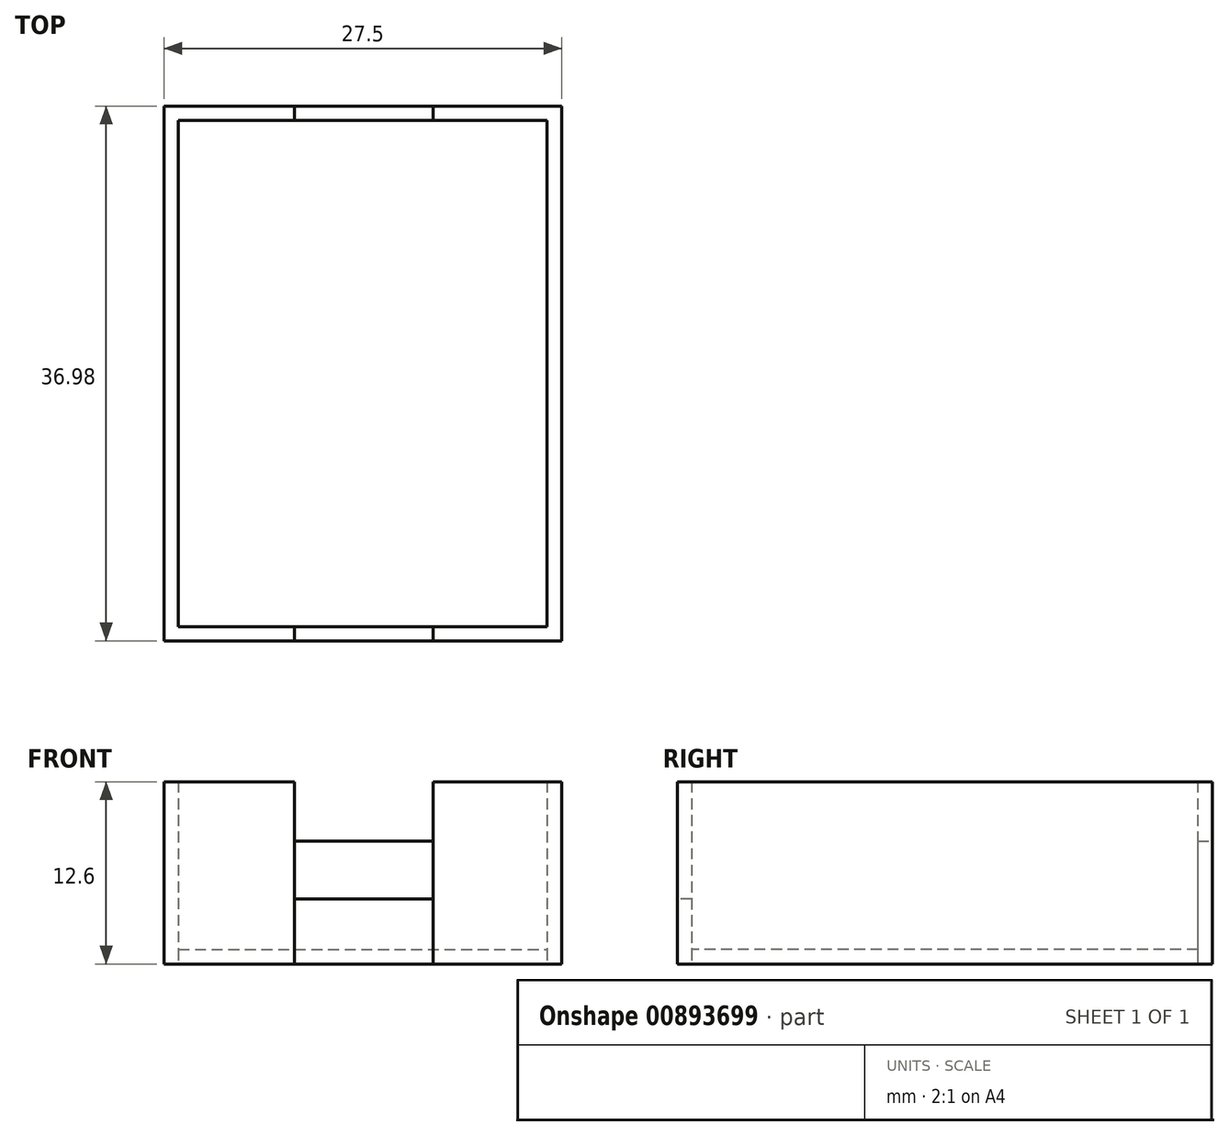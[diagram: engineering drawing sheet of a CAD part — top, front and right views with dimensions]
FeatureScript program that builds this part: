
annotation { "Feature Type Name" : "Feature", "Feature Type Description" : "" }
export const myFeature = defineFeature(function(context is Context, id is Id, definition is map)
    precondition{}
    {
        {
            var Q0;
            Q0=qCreatedBy(makeId("Top.planeOp"),FACE);
            var sketch = newSketch(context, id + "F0", { "sketchPlane" : qUnion([Q0])});
            skLineSegment(sketch, "E0.bottom", {"start": v(-11.86, 7.23) * mm, "end": v(13.64, 7.23) * mm});
            skLineSegment(sketch, "E0.top", {"start": v(-11.86, -27.77) * mm, "end": v(13.64, -27.77) * mm});
            skLineSegment(sketch, "E0.left", {"start": v(-11.86, 7.23) * mm, "end": v(-11.86, -27.77) * mm});
            skLineSegment(sketch, "E0.right", {"start": v(13.64, 7.23) * mm, "end": v(13.64, -27.77) * mm});
            skLineSegment(sketch, "E1", {"start": v(-12.86, 8.23) * mm, "end": v(13.62, 8.23) * mm});
            skLineSegment(sketch, "E2", {"start": v(-12.86, 8.23) * mm, "end": v(-12.86, -27.92) * mm});
            skLineSegment(sketch, "E3", {"start": v(14.64, -27.92) * mm, "end": v(14.64, 8.23) * mm});
            skLineSegment(sketch, "E4", {"start": v(-12.86, -28.75) * mm, "end": v(14.64, -28.75) * mm});
            skLineSegment(sketch, "E5", {"start": v(13.62, 8.23) * mm, "end": v(14.64, 8.23) * mm});
            skLineSegment(sketch, "E6", {"start": v(-12.86, -28.75) * mm, "end": v(-12.86, -27.92) * mm});
            skLineSegment(sketch, "E7", {"start": v(14.64, -28.75) * mm, "end": v(14.64, -27.92) * mm});
            skLineSegment(sketch, "E8", {"start": v(-3.85, 7.23) * mm, "end": v(-3.85, 8.23) * mm});
            skLineSegment(sketch, "E9", {"start": v(5.74, 7.23) * mm, "end": v(5.74, 8.23) * mm});
            skLineSegment(sketch, "E10", {"start": v(-3.85, -27.77) * mm, "end": v(-3.85, -28.75) * mm});
            skLineSegment(sketch, "E11", {"start": v(5.74, -27.77) * mm, "end": v(5.74, -28.75) * mm});
            skLineSegment(sketch, "E12", {"start": v(-3.85, 7.23) * mm, "end": v(-3.85, -26.5) * mm, "construction": true});
            skLineSegment(sketch, "E13", {"start": v(5.74, 7.23) * mm, "end": v(5.74, -26.5) * mm, "construction": true});
            skSolve(sketch);
        }
        {
            var Q0;
            {var subQ3=sQuery(id+"F0.wireOp",EDGE,"E0.right");Q0=makeQuery(id+"F0.imprint","IMPRINT",FACE,{"disambiguationData":[TD([[makeQuery(id+"F0.imprint","IMPRINT",EDGE,{"derivedFrom":subQ3}),1.0]])]});}
            extrude(context, id + "F1", {"entities" : qUnion([Q0]), "depth" : 12.6 * mm, "offsetDistance" : 25 * mm});
        }
        {
            var Q0;
            {var subQ0=sQuery(id+"F0.wireOp",EDGE,"E0.left");Q0=makeQuery(id+"F0.imprint","IMPRINT",FACE,{"disambiguationData":[TD([[makeQuery(id+"F0.imprint","IMPRINT",EDGE,{"derivedFrom":subQ0}),-1.0]])]});}
            extrude(context, id + "F2", {"entities" : qUnion([Q0]), "depth" : 12.6 * mm, "offsetDistance" : 25 * mm});
        }
        {
            var Q0;
            {var subQ0=sQuery(id+"F0.wireOp",EDGE,"E10");Q0=makeQuery(id+"F0.imprint","IMPRINT",FACE,{"disambiguationData":[TD([[makeQuery(id+"F0.imprint","IMPRINT",EDGE,{"derivedFrom":subQ0}),1.0]])]});}
            extrude(context, id + "F3", {"entities" : qUnion([Q0]), "depth" : 4.5 * mm, "offsetDistance" : 25 * mm});
        }
        {
            var Q0;
            {var subQ0=sQuery(id+"F0.wireOp",EDGE,"E8");Q0=makeQuery(id+"F0.imprint","IMPRINT",FACE,{"disambiguationData":[TD([[makeQuery(id+"F0.imprint","IMPRINT",EDGE,{"derivedFrom":subQ0}),-1.0]])]});}
            extrude(context, id + "F4", {"entities" : qUnion([Q0]), "depth" : 8.5 * mm, "offsetDistance" : 25 * mm});
        }
        {
            var Q0;
            {var subQ0=sQuery(id+"F0.wireOp",EDGE,"E0.left");Q0=makeQuery(id+"F0.imprint","IMPRINT",FACE,{"disambiguationData":[TD([[makeQuery(id+"F0.imprint","IMPRINT",EDGE,{"derivedFrom":subQ0}),1.0]])]});}
            extrude(context, id + "F5", {"entities" : qUnion([Q0]), "depth" : 1 * mm, "offsetDistance" : 25 * mm});
        }
    });
